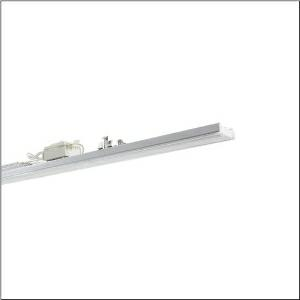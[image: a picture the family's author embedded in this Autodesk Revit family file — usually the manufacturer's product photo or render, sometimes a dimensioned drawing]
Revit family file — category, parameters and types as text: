
# Revit family: licross_r__11_recessed_mo_51tl12cn49xg_4efb
name_source: partatom
category: Lighting Fixtures
units: mm (PartAtom-declared; Revit-internal decimal feet)

## family parameters
Cut with Voids When Loaded = No
Host = Face
Light Source = No
Part Type = Normal
Room Calculation Point = No
Round Connector Dimension = Use Diameter
Shared = No

## types (1)
- --- (1 x LED, 9310 lm, 49.3 W, 4000K)
    Apparent Load = 49 VA
    CIE Flux Codes = 67 92 99 100 100
    Color Rendering = 80
    Color Temperature = 4000K
    Default Elevation = 1800 mm
    Description = Licross® 11 Recessed MO, luminaire insert, of sheet steel, coil coated, white, length: 1.500mm, width: 66mm, height: 67mm, LED rated luminous flux: 9.310lm, light colour: 840, control gear: ON/OFF Multilumen, CLOi, with plug, 3-pole, with phase selection, mains connection: 220..240V, AC, 50/60Hz, start of lifetime: 49W, end of service life: 55W, internal wiring halogen-free, primary optical cover: cover, of PMMA, light emission: direct distribution, primary light characteristic: symmetric, protection rating (complete): IP40, insulation class (complete): insulation class I (protective earthing), certification: CE, ENEC, VDE, UKCA, protection symbol: D if used in an environment without relevant dust loads with corresponding accessories, impact resistance: IK06, permissible ambient temperature for indoor applications: -35..+40°C, corresponds to IFS (International Featured Standards) requirements for safety and quality in the food industry, reducing of maximum allowable ambient temperature of 5°C with ceiling mounting, LABS conformity tested according to VDMA 24364:2018-05, packaging unit: 1 piece
    Height = 58 mm
    Lamp = 1 x LED
    Lamp Light Flux = 9310 lm
    Lamp Power = 49.3 W
    Lamp count = 1
    Length = 1500 mm
    Luminous efficacy = 189 lm/W
    Manufacturer = Siteco
    ModVariant = No
    Model = 51TL12CN49XG
    Mounting Place = Ceiling
    Mounting Type = Pendant
    Number of Poles = 1
    OnlyDefault = Yes
    Power Factor = 1
    Product Name = Licross® 11 Recessed MO
    Product group = luminaire insert | ceiling pendant
    ProductGroupID = 902
    Protection Class = Protection class I
    Protection Degree = IP 40
    RLX_Detail_Level = 1
    RLX_Emergency_Light_Flux = 0 lm
    RLX_Emergency_Type = 0
    RLX_Emergency_Type_DB = No
    RlxData = <blob elided: 22229 chars, md5=8a80e933>
    Socket = socket
    Standby Power = 0 W
    System Light Flux = 9310 lm
    System Power = 49 W
    Type Comments = factory setting: luminous flux: 100 % | (A | C | E) | 113 mA
    Type Image = l_1296930.jpg
    URL = http://relux.com
    VarID = @adj_107071
    Voltage = 0 V
    Weight = 0.00 kg
    Width = 66 mm

## geometry (parser evidence)
native form markers: Blend x4, Sweep x13
no freeform markers — native parametric forms only
